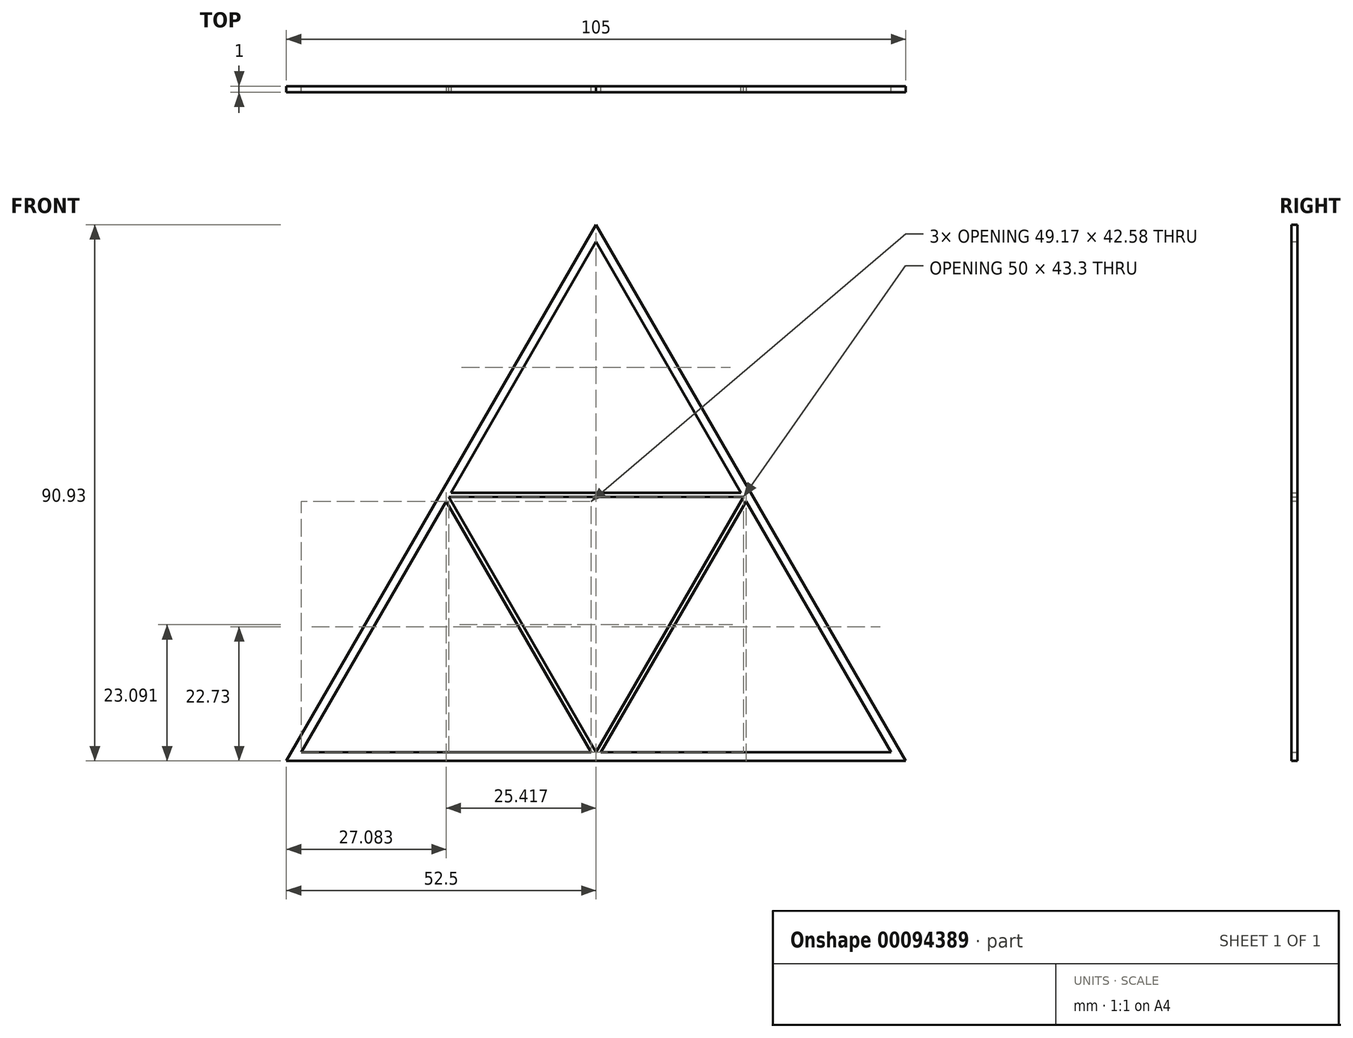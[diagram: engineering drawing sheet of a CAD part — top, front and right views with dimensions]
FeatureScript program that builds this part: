
annotation { "Feature Type Name" : "Feature", "Feature Type Description" : "" }
export const myFeature = defineFeature(function(context is Context, id is Id, definition is map)
    precondition{}
    {
        {
            var Q0;
            Q0=qCreatedBy(makeId("Front.planeOp"),FACE);
            var sketch = newSketch(context, id + "F0", { "sketchPlane" : qUnion([Q0])});
            skLineSegment(sketch, "E0", {"start": v(-50, 0) * mm, "end": v(50, 0) * mm});
            skLineSegment(sketch, "E1", {"start": v(50, 0) * mm, "end": v(0, 86.6) * mm});
            skLineSegment(sketch, "E2", {"start": v(0, 86.6) * mm, "end": v(-50, 0) * mm});
            skLineSegment(sketch, "E3", {"start": v(0, 89.49) * mm, "end": v(52.5, -1.44) * mm});
            skLineSegment(sketch, "E4", {"start": v(0, 89.49) * mm, "end": v(-52.5, -1.44) * mm});
            skLineSegment(sketch, "E5", {"start": v(-52.5, -1.44) * mm, "end": v(52.5, -1.44) * mm});
            skLineSegment(sketch, "E6", {"start": v(0, 86.6) * mm, "end": v(0, 89.49) * mm, "construction": true});
            skLineSegment(sketch, "E7", {"start": v(-50, 0) * mm, "end": v(-52.5, -1.44) * mm, "construction": true});
            skLineSegment(sketch, "E8", {"start": v(50, 0) * mm, "end": v(52.5, -1.44) * mm, "construction": true});
            skSolve(sketch);
        }
        {
            var Q0;
            Q0=makeQuery(id+"F0.imprint","IMPRINT",FACE,{"disambiguationData":[TD([[makeQuery(id+"F0.imprint","IMPRINT",EDGE,{"derivedFrom":sQuery(id+"F0.wireOp",EDGE,"E0")}),-1.0]])]});
            extrude(context, id + "F1", {"entities" : qUnion([Q0]), "depth" : 1 * mm});
        }
        {
            var Q0;
            Q0=qCreatedBy(makeId("Front.planeOp"),FACE);
            var sketch = newSketch(context, id + "F2", { "sketchPlane" : qUnion([Q0])});
            skLineSegment(sketch, "E9", {"start": v(0, 0) * mm, "end": v(25, 43.3) * mm});
            skLineSegment(sketch, "E10", {"start": v(0, 0) * mm, "end": v(-25, 43.3) * mm});
            skLineSegment(sketch, "E11", {"start": v(-25, 43.3) * mm, "end": v(25, 43.3) * mm});
            skLineSegment(sketch, "E12", {"start": v(-26.25, 44.02) * mm, "end": v(0, -1.44) * mm});
            skLineSegment(sketch, "E13", {"start": v(-26.25, 44.02) * mm, "end": v(26.25, 44.02) * mm});
            skLineSegment(sketch, "E14", {"start": v(26.25, 44.02) * mm, "end": v(0, -1.44) * mm});
            skSolve(sketch);
        }
        {
            var Q0;
            Q0=makeQuery(id+"F2.imprint","IMPRINT",FACE,{"disambiguationData":[TD([[makeQuery(id+"F2.imprint","IMPRINT",EDGE,{"derivedFrom":sQuery(id+"F2.wireOp",EDGE,"E9")}),-1.0]])]});
            extrude(context, id + "F3", {"entities" : qUnion([Q0]), "operationType" : NewBodyOperationType.ADD, "depth" : 1 * mm});
        }
    });
